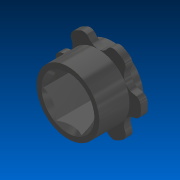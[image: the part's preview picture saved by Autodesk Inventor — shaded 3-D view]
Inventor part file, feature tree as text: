
AUTODESK INVENTOR PART (.ipt)
format: ipt  version: 2022.2 (Build 262287000, 287)  size: 154,112 bytes
history: native  units: in
note: dims shown in document units (in); Inventor stores cm internally (conversion verified against a paired STEP export)
features: fillet x1
ambient origin geometry x8: Origin, YZ Plane, XZ Plane, XY Plane, X Axis, Y Axis, Z Axis, Center Point
bodies: Solid1 (feature_tree)
feature tree (1):
  fillet  "Fillet1"  [1 undecoded]
note: 1 required parameter value undecoded (feature->parameter linkage not recoverable at this tier; creation-order binding heuristic only, values carry confidence <= 0.55)
